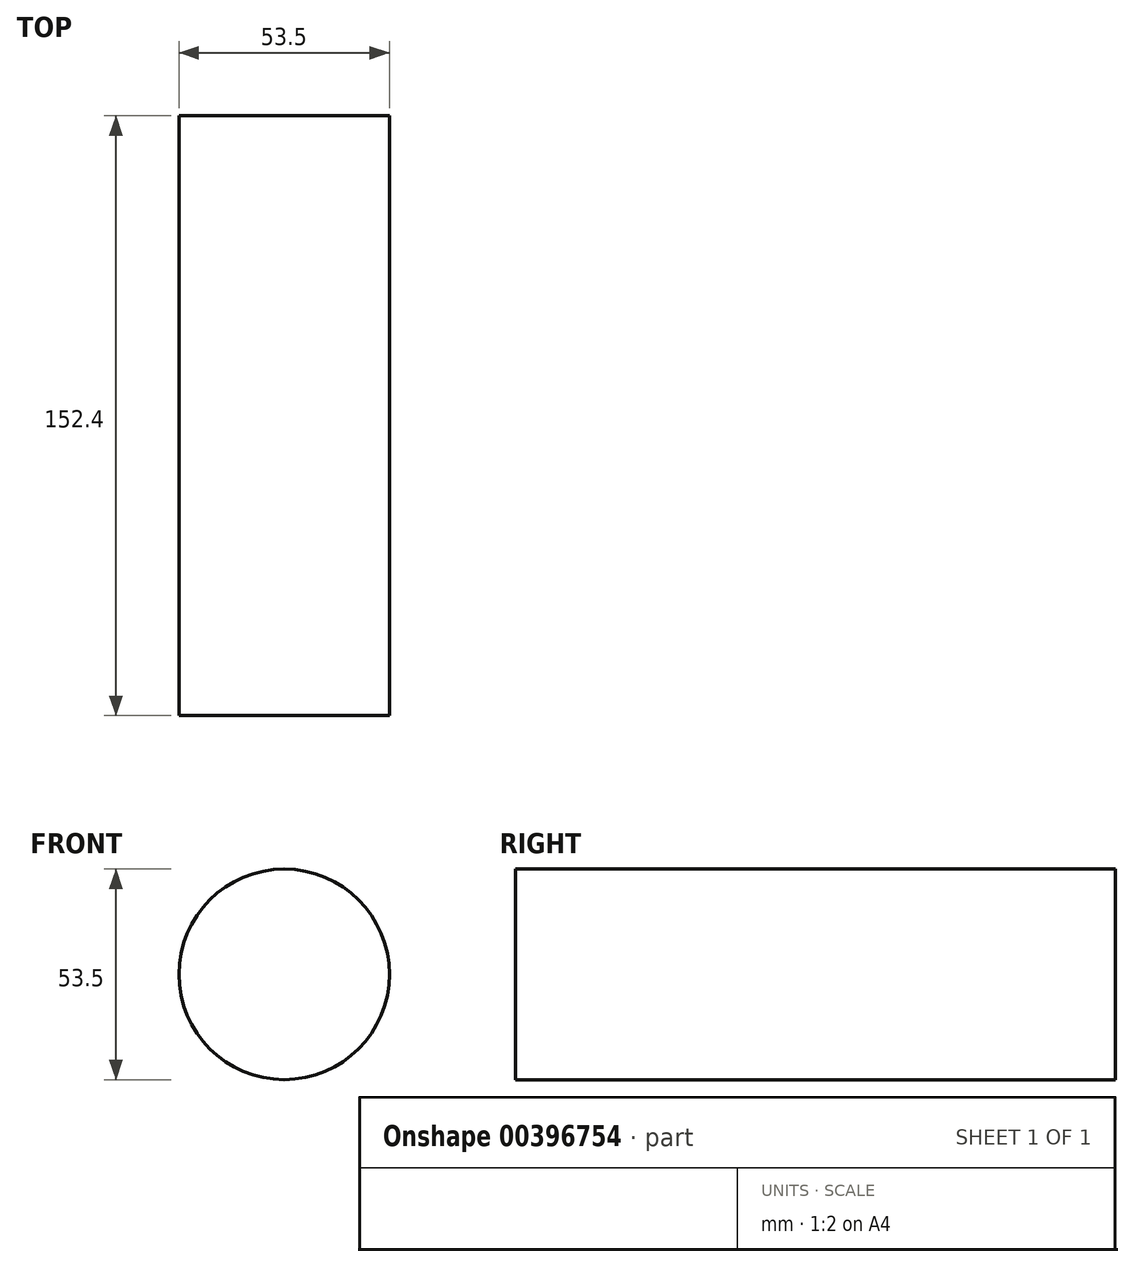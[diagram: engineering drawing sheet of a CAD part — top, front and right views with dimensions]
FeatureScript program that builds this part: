
annotation { "Feature Type Name" : "Feature", "Feature Type Description" : "" }
export const myFeature = defineFeature(function(context is Context, id is Id, definition is map)
    precondition{}
    {
        {
            var Q0;
            Q0=qCreatedBy(makeId("Front.planeOp"),FACE);
            var sketch = newSketch(context, id + "F0", { "sketchPlane" : qUnion([Q0])});
            skCircle(sketch, "E0", {"center": v(0, 0) * mm, "radius": 26.75 * mm});
            skSolve(sketch);
        }
        {
            var Q0;
            Q0=makeQuery(id+"F0.imprint","IMPRINT",FACE,{"disambiguationData":[TD([[makeQuery(id+"F0.imprint","IMPRINT",EDGE,{"derivedFrom":sQuery(id+"F0.wireOp",EDGE,"E0")}),1.0]])]});
            extrude(context, id + "F1", {"entities" : qUnion([Q0]), "depth" : 152.4 * mm});
        }
    });
